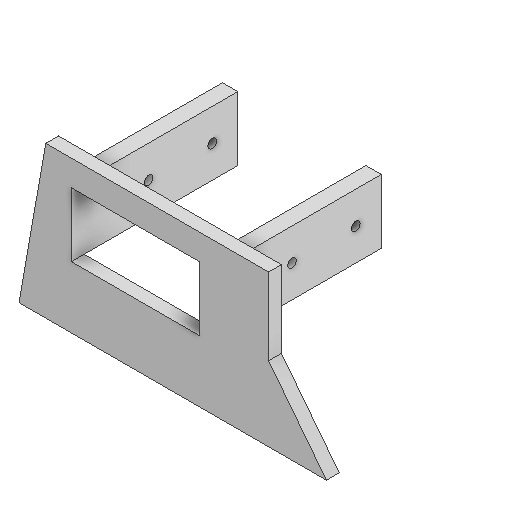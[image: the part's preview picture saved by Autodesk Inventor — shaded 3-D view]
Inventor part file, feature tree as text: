
AUTODESK INVENTOR PART (.ipt)
format: ipt  version: 2025.1 (Build 291241000, 241)  size: 151,552 bytes
history: native  units: mm
features: sketch x7, extrude x4, hole x3, other x1
ambient origin geometry x8: Origin, YZ Plane, XZ Plane, XY Plane, X Axis, Y Axis, Z Axis, Center Point
bodies: Body1 (feature_tree), Body2 (feature_tree)
feature tree (15):
  other  "Bryła1"
  extrude  "Wyciągnięcie proste1"  Depth=120.0mm
  extrude  "Wyciągnięcie proste2"  Depth=60.0mm
  extrude  "Wyciągnięcie proste3"  Depth=13.962634mm
  extrude  "Wyciągnięcie proste4"  Depth=60.0mm
  hole  "Otwór1"  [1 undecoded]
  hole  "Otwór2"  [1 undecoded]
  hole  "Otwór3"  [1 undecoded]
  sketch  "Szkic1"
  sketch  "Szkic2"
  sketch  "Szkic3"
  sketch  "Szkic4"
  sketch  "Szkic5"
  sketch  "Szkic7"
  sketch  "Szkic8"
note: 3 required parameter values undecoded (feature->parameter linkage not recoverable at this tier; creation-order binding heuristic only, values carry confidence <= 0.55)
